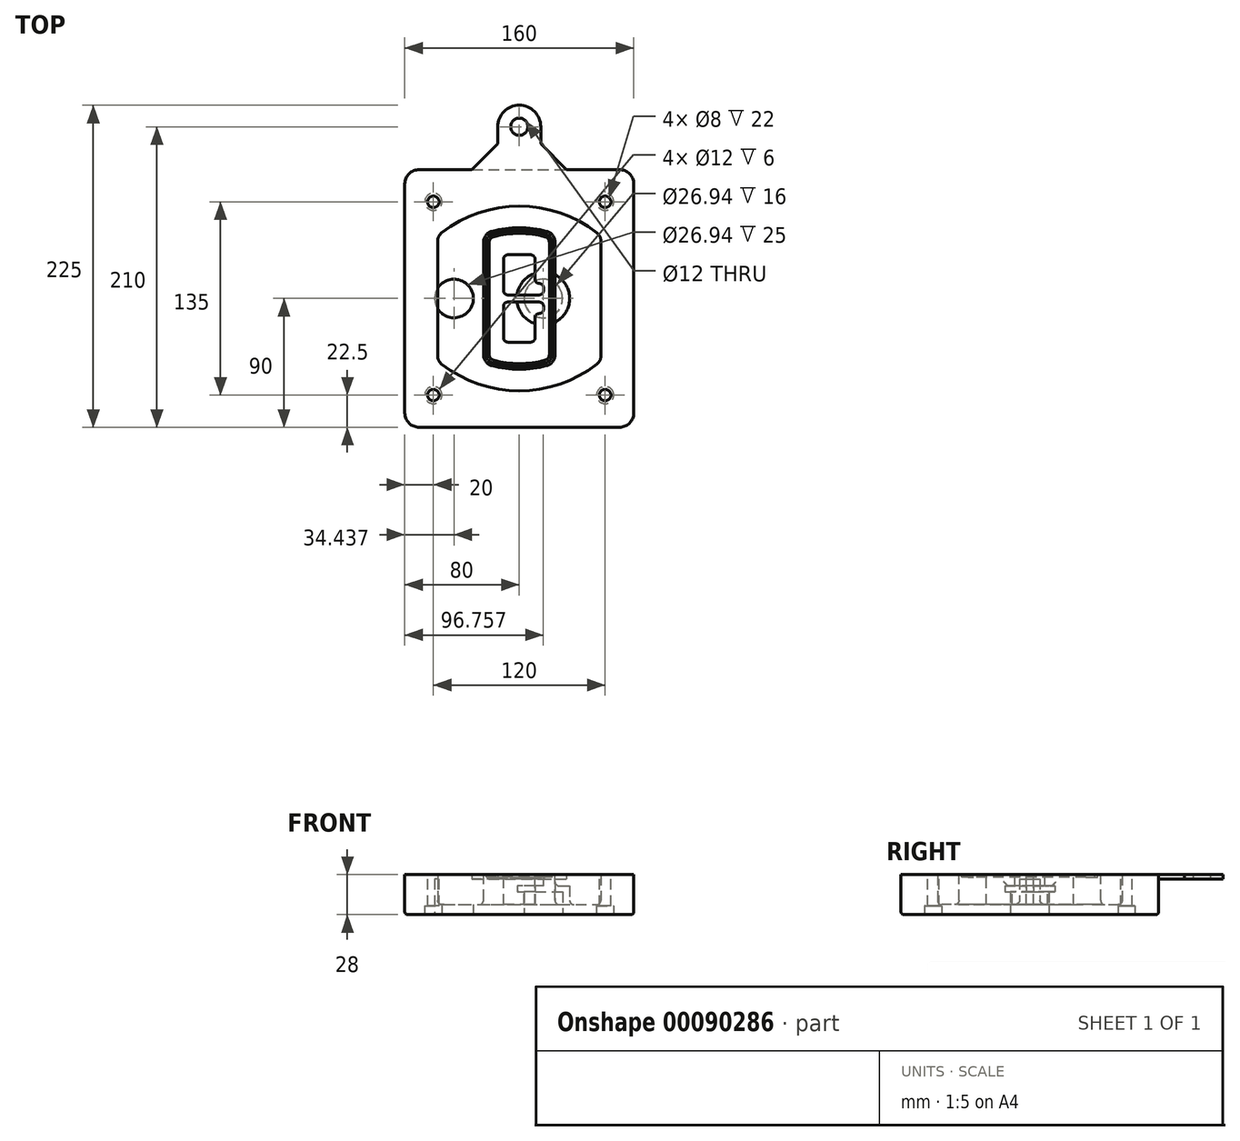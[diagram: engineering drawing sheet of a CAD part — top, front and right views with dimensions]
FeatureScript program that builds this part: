
annotation { "Feature Type Name" : "Feature", "Feature Type Description" : "" }
export const myFeature = defineFeature(function(context is Context, id is Id, definition is map)
    precondition{}
    {
        {
            var Q0;
            Q0=qCreatedBy(makeId("Top.planeOp"),FACE);
            var sketch = newSketch(context, id + "F0", { "sketchPlane" : qUnion([Q0])});
            skPoint(sketch, "E0.rect.middle", {"position": v(0, 0) * mm});
            skLineSegment(sketch, "E1.bottom", {"start": v(-70, -90) * mm, "end": v(70, -90) * mm});
            skLineSegment(sketch, "E1.top", {"start": v(-70, 90) * mm, "end": v(70, 90) * mm});
            skLineSegment(sketch, "E1.left", {"start": v(-80, -80) * mm, "end": v(-80, 80) * mm});
            skLineSegment(sketch, "E1.right", {"start": v(80, -80) * mm, "end": v(80, 80) * mm});
            skLineSegment(sketch, "E2", {"start": v(-80, 90) * mm, "end": v(80, -90) * mm, "construction": true});
            skLineSegment(sketch, "E3", {"start": v(80, 90) * mm, "end": v(-80, -90) * mm, "construction": true});
            skCircle(sketch, "E4", {"center": v(-60, 67.5) * mm, "radius": 4 * mm});
            skCircle(sketch, "E5", {"center": v(60, 67.5) * mm, "radius": 4 * mm});
            skCircle(sketch, "E6", {"center": v(60, -67.5) * mm, "radius": 4 * mm});
            skCircle(sketch, "E7", {"center": v(-60, -67.5) * mm, "radius": 4 * mm});
            skLineSegment(sketch, "E8", {"start": v(-60, 67.5) * mm, "end": v(60, 67.5) * mm, "construction": true});
            skLineSegment(sketch, "E9", {"start": v(60, 67.5) * mm, "end": v(60, -67.5) * mm, "construction": true});
            skLineSegment(sketch, "E10", {"start": v(60, -67.5) * mm, "end": v(-60, -67.5) * mm, "construction": true});
            skLineSegment(sketch, "E11", {"start": v(-60, -67.5) * mm, "end": v(-60, 67.5) * mm, "construction": true});
            skLineSegment(sketch, "E12", {"start": v(-60, 40.3) * mm, "end": v(-60, -40.3) * mm});
            skLineSegment(sketch, "E13", {"start": v(60, 40.3) * mm, "end": v(60, -40.3) * mm});
            skArc(sketch, "E14", {"start": v(56.15, 48.18) * mm, "mid": v(0, 67.5) * mm, "end": v(-56.15, 48.18) * mm});
            skArc(sketch, "E15", {"start": v(-56.15, -48.18) * mm, "mid": v(0, -67.5) * mm, "end": v(56.15, -48.18) * mm});
            skLineSegment(sketch, "E16", {"start": v(-60, 0) * mm, "end": v(60, 0) * mm, "construction": true});
            skPoint(sketch, "E17.visualSharp", {"position": v(-60, -45) * mm});
            skArc(sketch, "E17.filletArc", {"start": v(-60, -40.3) * mm, "mid": v(-58.99, -44.68) * mm, "end": v(-56.15, -48.18) * mm});
            skPoint(sketch, "E18.visualSharp", {"position": v(-60, 45) * mm});
            skArc(sketch, "E18.filletArc", {"start": v(-56.15, 48.18) * mm, "mid": v(-58.99, 44.68) * mm, "end": v(-60, 40.3) * mm});
            skPoint(sketch, "E19.visualSharp", {"position": v(60, 45) * mm});
            skArc(sketch, "E19.filletArc", {"start": v(60, 40.3) * mm, "mid": v(58.99, 44.68) * mm, "end": v(56.15, 48.18) * mm});
            skPoint(sketch, "E20.visualSharp", {"position": v(60, -45) * mm});
            skArc(sketch, "E20.filletArc", {"start": v(56.15, -48.18) * mm, "mid": v(58.99, -44.68) * mm, "end": v(60, -40.3) * mm});
            skPoint(sketch, "E21.visualSharp", {"position": v(-80, 90) * mm});
            skArc(sketch, "E21.filletArc", {"start": v(-70, 90) * mm, "mid": v(-77.07, 87.07) * mm, "end": v(-80, 80) * mm});
            skPoint(sketch, "E22.visualSharp", {"position": v(80, 90) * mm});
            skArc(sketch, "E22.filletArc", {"start": v(80, 80) * mm, "mid": v(77.07, 87.07) * mm, "end": v(70, 90) * mm});
            skPoint(sketch, "E23.visualSharp", {"position": v(80, -90) * mm});
            skArc(sketch, "E23.filletArc", {"start": v(70, -90) * mm, "mid": v(77.07, -87.07) * mm, "end": v(80, -80) * mm});
            skPoint(sketch, "E24.visualSharp", {"position": v(-80, -90) * mm});
            skArc(sketch, "E24.filletArc", {"start": v(-80, -80) * mm, "mid": v(-77.07, -87.07) * mm, "end": v(-70, -90) * mm});
            skArc(sketch, "E25.0", {"start": v(57, 40.3) * mm, "mid": v(56.3, 43.36) * mm, "end": v(54.3, 45.81) * mm});
            skLineSegment(sketch, "E25.1", {"start": v(57, 40.3) * mm, "end": v(57, -40.3) * mm});
            skArc(sketch, "E25.2", {"start": v(54.3, -45.81) * mm, "mid": v(56.3, -43.36) * mm, "end": v(57, -40.3) * mm});
            skArc(sketch, "E25.3", {"start": v(-54.3, -45.81) * mm, "mid": v(0, -64.5) * mm, "end": v(54.3, -45.81) * mm});
            skArc(sketch, "E25.4", {"start": v(-57, -40.3) * mm, "mid": v(-56.3, -43.36) * mm, "end": v(-54.3, -45.81) * mm});
            skArc(sketch, "E25.5", {"start": v(54.3, 45.81) * mm, "mid": v(0, 64.5) * mm, "end": v(-54.3, 45.81) * mm});
            skLineSegment(sketch, "E25.6", {"start": v(-57, 40.3) * mm, "end": v(-57, -40.3) * mm});
            skArc(sketch, "E25.7", {"start": v(-54.3, 45.81) * mm, "mid": v(-56.3, 43.36) * mm, "end": v(-57, 40.3) * mm});
            skArc(sketch, "E26.0", {"start": v(-58.62, 51.33) * mm, "mid": v(-62.58, 46.43) * mm, "end": v(-64, 40.3) * mm});
            skArc(sketch, "E26.1", {"start": v(58.62, 51.33) * mm, "mid": v(0, 71.5) * mm, "end": v(-58.62, 51.33) * mm});
            skArc(sketch, "E26.2", {"start": v(64, 40.3) * mm, "mid": v(62.58, 46.43) * mm, "end": v(58.62, 51.33) * mm});
            skLineSegment(sketch, "E26.3", {"start": v(64, 40.3) * mm, "end": v(64, -40.3) * mm});
            skArc(sketch, "E26.4", {"start": v(58.62, -51.33) * mm, "mid": v(62.58, -46.43) * mm, "end": v(64, -40.3) * mm});
            skLineSegment(sketch, "E26.5", {"start": v(-64, 40.3) * mm, "end": v(-64, -40.3) * mm});
            skArc(sketch, "E26.6", {"start": v(-58.62, -51.33) * mm, "mid": v(0, -71.5) * mm, "end": v(58.62, -51.33) * mm});
            skArc(sketch, "E26.7", {"start": v(-64, -40.3) * mm, "mid": v(-62.58, -46.43) * mm, "end": v(-58.62, -51.33) * mm});
            skSolve(sketch);
        }
        {
            var Q0;
            Q0=makeQuery(id+"F0.imprint","IMPRINT",FACE,{"disambiguationData":[TD([[makeQuery(id+"F0.imprint","IMPRINT",EDGE,{"derivedFrom":sQuery(id+"F0.wireOp",EDGE,"E1.bottom")}),1.0]])]});
            var Q1;
            Q1=makeQuery(id+"F0.imprint","IMPRINT",FACE,{"disambiguationData":[TD([[makeQuery(id+"F0.imprint","IMPRINT",EDGE,{"derivedFrom":sQuery(id+"F0.wireOp",EDGE,"E12")}),1.0]])]});
            var Q2;
            Q2=makeQuery(id+"F0.imprint","IMPRINT",FACE,{"disambiguationData":[TD([[makeQuery(id+"F0.imprint","IMPRINT",EDGE,{"derivedFrom":sQuery(id+"F0.wireOp",EDGE,"E25.0")}),1.0]])]});
            var Q3;
            Q3=makeQuery(id+"F0.imprint","IMPRINT",FACE,{"disambiguationData":[TD([[makeQuery(id+"F0.imprint","IMPRINT",EDGE,{"derivedFrom":sQuery(id+"F0.wireOp",EDGE,"E12")}),-1.0]])]});
            extrude(context, id + "F1", {"entities" : qUnion([Q0, Q1, Q2, Q3]), "oppositeDirection" : true, "depth" : 25 * mm});
        }
        {
            var Q0;
            Q0=makeQuery(id+"F0.imprint","IMPRINT",FACE,{"disambiguationData":[TD([[makeQuery(id+"F0.imprint","IMPRINT",EDGE,{"derivedFrom":sQuery(id+"F0.wireOp",EDGE,"E12")}),1.0]])]});
            extrude(context, id + "F2", {"entities" : qUnion([Q0]), "operationType" : NewBodyOperationType.ADD, "depth" : 3 * mm});
        }
        {
            var Q0;
            Q0=makeQuery(id+"F0.imprint","IMPRINT",FACE,{"disambiguationData":[TD([[makeQuery(id+"F0.imprint","IMPRINT",EDGE,{"derivedFrom":sQuery(id+"F0.wireOp",EDGE,"E25.0")}),1.0]])]});
            extrude(context, id + "F3", {"entities" : qUnion([Q0]), "operationType" : NewBodyOperationType.REMOVE, "oppositeDirection" : true, "depth" : 18 * mm});
        }
        {
            var Q0;
            Q0=makeQuery(id+"F2.opExtrude","CAP_FACE",FACE,{"disambiguationData":[OSD([sQuery(id+"F0.wireOp",EDGE,"E12"),sQuery(id+"F0.wireOp",EDGE,"E13"),sQuery(id+"F0.wireOp",EDGE,"E14"),sQuery(id+"F0.wireOp",EDGE,"E15"),sQuery(id+"F0.wireOp",EDGE,"E17.filletArc"),sQuery(id+"F0.wireOp",EDGE,"E18.filletArc"),sQuery(id+"F0.wireOp",EDGE,"E19.filletArc"),sQuery(id+"F0.wireOp",EDGE,"E20.filletArc"),sQuery(id+"F0.wireOp",EDGE,"E25.0"),sQuery(id+"F0.wireOp",EDGE,"E25.1"),sQuery(id+"F0.wireOp",EDGE,"E25.2"),sQuery(id+"F0.wireOp",EDGE,"E25.3"),sQuery(id+"F0.wireOp",EDGE,"E25.4"),sQuery(id+"F0.wireOp",EDGE,"E25.5"),sQuery(id+"F0.wireOp",EDGE,"E25.6"),sQuery(id+"F0.wireOp",EDGE,"E25.7")])],"isStart":false});
            var sketch = newSketch(context, id + "F4", { "sketchPlane" : qUnion([Q0])});
            skArc(sketch, "E27.0", {"start": v(-19.08, -46.97) * mm, "mid": v(0, -49.5) * mm, "end": v(19.08, -46.97) * mm});
            skArc(sketch, "E28.0", {"start": v(19.08, 46.97) * mm, "mid": v(0, 49.5) * mm, "end": v(-19.08, 46.97) * mm});
            skLineSegment(sketch, "E29", {"start": v(-25, 39.25) * mm, "end": v(-25, -39.25) * mm});
            skLineSegment(sketch, "E30", {"start": v(25, 39.25) * mm, "end": v(25, -39.25) * mm});
            skLineSegment(sketch, "E31", {"start": v(-25, 45.1) * mm, "end": v(25, 45.1) * mm, "construction": true});
            skLineSegment(sketch, "E32", {"start": v(-25, -45.1) * mm, "end": v(25, -45.1) * mm, "construction": true});
            skPoint(sketch, "E33.visualSharp", {"position": v(-25, 45.1) * mm});
            skArc(sketch, "E33.filletArc", {"start": v(-19.08, 46.97) * mm, "mid": v(-23.35, 44.11) * mm, "end": v(-25, 39.25) * mm});
            skPoint(sketch, "E34.visualSharp", {"position": v(25, 45.1) * mm});
            skArc(sketch, "E34.filletArc", {"start": v(25, 39.25) * mm, "mid": v(23.35, 44.11) * mm, "end": v(19.08, 46.97) * mm});
            skPoint(sketch, "E35.visualSharp", {"position": v(25, -45.1) * mm});
            skArc(sketch, "E35.filletArc", {"start": v(19.08, -46.97) * mm, "mid": v(23.35, -44.11) * mm, "end": v(25, -39.25) * mm});
            skPoint(sketch, "E36.visualSharp", {"position": v(-25, -45.1) * mm});
            skArc(sketch, "E36.filletArc", {"start": v(-25, -39.25) * mm, "mid": v(-23.35, -44.11) * mm, "end": v(-19.08, -46.97) * mm});
            skArc(sketch, "E37.0", {"start": v(54.3, 45.81) * mm, "mid": v(0, 64.5) * mm, "end": v(-54.3, 45.81) * mm});
            skArc(sketch, "E37.1", {"start": v(-54.3, 45.81) * mm, "mid": v(-56.3, 43.36) * mm, "end": v(-57, 40.3) * mm});
            skLineSegment(sketch, "E37.2", {"start": v(-57, 40.3) * mm, "end": v(-57, -40.3) * mm});
            skArc(sketch, "E37.3", {"start": v(-57, -40.3) * mm, "mid": v(-56.3, -43.36) * mm, "end": v(-54.3, -45.81) * mm});
            skArc(sketch, "E37.4", {"start": v(-54.3, -45.81) * mm, "mid": v(0, -64.5) * mm, "end": v(54.3, -45.81) * mm});
            skArc(sketch, "E37.5", {"start": v(54.3, -45.81) * mm, "mid": v(56.3, -43.36) * mm, "end": v(57, -40.3) * mm});
            skLineSegment(sketch, "E37.6", {"start": v(57, 40.3) * mm, "end": v(57, -40.3) * mm});
            skArc(sketch, "E37.7", {"start": v(57, 40.3) * mm, "mid": v(56.3, 43.36) * mm, "end": v(54.3, 45.81) * mm});
            skLineSegment(sketch, "E38.0", {"start": v(23, 39.25) * mm, "end": v(23, -39.25) * mm});
            skArc(sketch, "E38.1", {"start": v(18.56, -45.04) * mm, "mid": v(21.76, -42.9) * mm, "end": v(23, -39.25) * mm});
            skArc(sketch, "E38.2", {"start": v(-18.56, -45.04) * mm, "mid": v(0, -47.5) * mm, "end": v(18.56, -45.04) * mm});
            skArc(sketch, "E38.3", {"start": v(-23, -39.25) * mm, "mid": v(-21.76, -42.9) * mm, "end": v(-18.56, -45.04) * mm});
            skLineSegment(sketch, "E38.4", {"start": v(-23, 39.25) * mm, "end": v(-23, -39.25) * mm});
            skArc(sketch, "E38.5", {"start": v(23, 39.25) * mm, "mid": v(21.76, 42.9) * mm, "end": v(18.56, 45.04) * mm});
            skArc(sketch, "E38.6", {"start": v(-18.56, 45.04) * mm, "mid": v(-21.76, 42.9) * mm, "end": v(-23, 39.25) * mm});
            skArc(sketch, "E38.7", {"start": v(18.56, 45.04) * mm, "mid": v(0, 47.5) * mm, "end": v(-18.56, 45.04) * mm});
            skArc(sketch, "E39.0", {"start": v(21, 39.25) * mm, "mid": v(20.18, 41.68) * mm, "end": v(18.04, 43.1) * mm});
            skLineSegment(sketch, "E39.1", {"start": v(21, 39.25) * mm, "end": v(21, -39.25) * mm});
            skArc(sketch, "E39.2", {"start": v(18.04, -43.1) * mm, "mid": v(20.18, -41.68) * mm, "end": v(21, -39.25) * mm});
            skArc(sketch, "E39.3", {"start": v(-18.04, -43.1) * mm, "mid": v(0, -45.5) * mm, "end": v(18.04, -43.1) * mm});
            skArc(sketch, "E39.4", {"start": v(-21, -39.25) * mm, "mid": v(-20.18, -41.68) * mm, "end": v(-18.04, -43.1) * mm});
            skArc(sketch, "E39.5", {"start": v(18.04, 43.1) * mm, "mid": v(0, 45.5) * mm, "end": v(-18.04, 43.1) * mm});
            skLineSegment(sketch, "E39.6", {"start": v(-21, 39.25) * mm, "end": v(-21, -39.25) * mm});
            skArc(sketch, "E39.7", {"start": v(-18.04, 43.1) * mm, "mid": v(-20.18, 41.68) * mm, "end": v(-21, 39.25) * mm});
            skLineSegment(sketch, "E40", {"start": v(-25, 0) * mm, "end": v(25, 0) * mm, "construction": true});
            skLineSegment(sketch, "E41", {"start": v(-11, 5.5) * mm, "end": v(-11, 27.5) * mm});
            skLineSegment(sketch, "E42", {"start": v(-8, 30.5) * mm, "end": v(8, 30.5) * mm});
            skLineSegment(sketch, "E43", {"start": v(11, 27.5) * mm, "end": v(11, 13.5) * mm});
            skLineSegment(sketch, "E44", {"start": v(14, 10.5) * mm, "end": v(14, 10.5) * mm});
            skLineSegment(sketch, "E45", {"start": v(17, 7.5) * mm, "end": v(17, 5.5) * mm});
            skLineSegment(sketch, "E46", {"start": v(14, 2.5) * mm, "end": v(-8, 2.5) * mm});
            skPoint(sketch, "E47.visualSharp", {"position": v(-11, 30.5) * mm});
            skArc(sketch, "E47.filletArc", {"start": v(-8, 30.5) * mm, "mid": v(-10.12, 29.62) * mm, "end": v(-11, 27.5) * mm});
            skPoint(sketch, "E48.visualSharp", {"position": v(11, 30.5) * mm});
            skArc(sketch, "E48.filletArc", {"start": v(11, 27.5) * mm, "mid": v(10.12, 29.62) * mm, "end": v(8, 30.5) * mm});
            skPoint(sketch, "E49.visualSharp", {"position": v(11, 10.5) * mm});
            skArc(sketch, "E49.filletArc", {"start": v(11, 13.5) * mm, "mid": v(11.88, 11.38) * mm, "end": v(14, 10.5) * mm});
            skPoint(sketch, "E50.visualSharp", {"position": v(17, 10.5) * mm});
            skArc(sketch, "E50.filletArc", {"start": v(17, 7.5) * mm, "mid": v(16.12, 9.62) * mm, "end": v(14, 10.5) * mm});
            skPoint(sketch, "E51.visualSharp", {"position": v(17, 2.5) * mm});
            skArc(sketch, "E51.filletArc", {"start": v(14, 2.5) * mm, "mid": v(16.12, 3.38) * mm, "end": v(17, 5.5) * mm});
            skPoint(sketch, "E52.visualSharp", {"position": v(-11, 2.5) * mm});
            skArc(sketch, "E52.filletArc", {"start": v(-11, 5.5) * mm, "mid": v(-10.12, 3.38) * mm, "end": v(-8, 2.5) * mm});
            skLineSegment(sketch, "E53.0.MirrorCS", {"start": v(14, -2.5) * mm, "end": v(-8, -2.5) * mm});
            skArc(sketch, "E54.0.MirrorCS", {"start": v(-11, -5.5) * mm, "mid": v(-10.12, -3.38) * mm, "end": v(-8, -2.5) * mm});
            skLineSegment(sketch, "E55.0.MirrorCS", {"start": v(-11, -5.5) * mm, "end": v(-11, -27.5) * mm});
            skArc(sketch, "E56.0.MirrorCS", {"start": v(-8, -30.5) * mm, "mid": v(-10.12, -29.62) * mm, "end": v(-11, -27.5) * mm});
            skLineSegment(sketch, "E57.0.MirrorCS", {"start": v(-8, -30.5) * mm, "end": v(8, -30.5) * mm});
            skArc(sketch, "E58.0.MirrorCS", {"start": v(11, -27.5) * mm, "mid": v(10.12, -29.62) * mm, "end": v(8, -30.5) * mm});
            skLineSegment(sketch, "E59.0.MirrorCS", {"start": v(11, -27.5) * mm, "end": v(11, -13.5) * mm});
            skArc(sketch, "E60.0.MirrorCS", {"start": v(11, -13.5) * mm, "mid": v(11.88, -11.38) * mm, "end": v(14, -10.5) * mm});
            skArc(sketch, "E61.0.MirrorCS", {"start": v(17, -7.5) * mm, "mid": v(16.12, -9.62) * mm, "end": v(14, -10.5) * mm});
            skLineSegment(sketch, "E62.0.MirrorCS", {"start": v(17, -7.5) * mm, "end": v(17, -5.5) * mm});
            skArc(sketch, "E63.0.MirrorCS", {"start": v(14, -2.5) * mm, "mid": v(16.12, -3.38) * mm, "end": v(17, -5.5) * mm});
            skSolve(sketch);
        }
        {
            var Q0;
            Q0=makeQuery(id+"F4.imprint","IMPRINT",FACE,{"disambiguationData":[TD([[makeQuery(id+"F4.imprint","IMPRINT",EDGE,{"derivedFrom":sQuery(id+"F4.wireOp",EDGE,"E27.0")}),1.0]])]});
            var Q1;
            Q1=makeQuery(id+"F4.imprint","IMPRINT",FACE,{"disambiguationData":[TD([[makeQuery(id+"F4.imprint","IMPRINT",EDGE,{"derivedFrom":sQuery(id+"F4.wireOp",EDGE,"E38.0")}),-1.0]])]});
            var Q2;
            Q2=makeQuery(id+"F4.imprint","IMPRINT",FACE,{"disambiguationData":[TD([[makeQuery(id+"F4.imprint","IMPRINT",EDGE,{"derivedFrom":sQuery(id+"F4.wireOp",EDGE,"E39.0")}),1.0]])]});
            extrude(context, id + "F5", {"entities" : qUnion([Q0, Q1, Q2]), "operationType" : NewBodyOperationType.ADD, "endBound" : BoundingType.UP_TO_NEXT, "oppositeDirection" : true, "depth" : 25 * mm});
        }
        {
            var Q0;
            Q0=makeQuery(id+"F4.imprint","IMPRINT",FACE,{"disambiguationData":[TD([[makeQuery(id+"F4.imprint","IMPRINT",EDGE,{"derivedFrom":sQuery(id+"F4.wireOp",EDGE,"E38.0")}),-1.0]])]});
            extrude(context, id + "F6", {"entities" : qUnion([Q0]), "operationType" : NewBodyOperationType.REMOVE, "oppositeDirection" : true, "depth" : 2 * mm});
        }
        {
            var Q0;
            Q0=makeQuery(id+"F1.opExtrude","CAP_FACE",FACE,{"disambiguationData":[OSD([sQuery(id+"F0.wireOp",EDGE,"E1.bottom"),sQuery(id+"F0.wireOp",EDGE,"E1.top"),sQuery(id+"F0.wireOp",EDGE,"E1.left"),sQuery(id+"F0.wireOp",EDGE,"E1.right"),sQuery(id+"F0.wireOp",EDGE,"E4"),sQuery(id+"F0.wireOp",EDGE,"E5"),sQuery(id+"F0.wireOp",EDGE,"E6"),sQuery(id+"F0.wireOp",EDGE,"E7"),sQuery(id+"F0.wireOp",EDGE,"E21.filletArc"),sQuery(id+"F0.wireOp",EDGE,"E22.filletArc"),sQuery(id+"F0.wireOp",EDGE,"E23.filletArc"),sQuery(id+"F0.wireOp",EDGE,"E24.filletArc")])],"isStart":false});
            var sketch = newSketch(context, id + "F7", { "sketchPlane" : qUnion([Q0])});
            skCircle(sketch, "E64", {"center": v(16.76, 0) * mm, "radius": 13.47 * mm});
            skCircle(sketch, "E65", {"center": v(-45.56, 0) * mm, "radius": 13.47 * mm});
            skLineSegment(sketch, "E66", {"start": v(80, 0) * mm, "end": v(-80, 0) * mm});
            skCircle(sketch, "E67", {"center": v(16.76, 0) * mm, "radius": 18.47 * mm});
            skCircle(sketch, "E68", {"center": v(60, -67.5) * mm, "radius": 6 * mm});
            skCircle(sketch, "E69", {"center": v(-60, -67.5) * mm, "radius": 6 * mm});
            skCircle(sketch, "E70", {"center": v(-60, 67.5) * mm, "radius": 6 * mm});
            skCircle(sketch, "E71", {"center": v(60, 67.5) * mm, "radius": 6 * mm});
            skSolve(sketch);
        }
        {
            var Q0;
            {var subQ1=sQuery(id+"F7.wireOp",EDGE,"E66");var subQ4=sQuery(id+"F7.wireOp",EDGE,"E64");var subQ6=makeQuery(id+"F7.imprint","INTERSECT",VERTEX,{"disambiguationData":[OD(0.0)],"derivedFrom":[subQ4,subQ1]});Q0=makeQuery(id+"F7.imprint","IMPRINT",FACE,{"disambiguationData":[TD([[makeQuery(id+"F7.imprint","IMPRINT",EDGE,{"disambiguationData":[TD([[subQ6,-1.0]])],"derivedFrom":subQ4}),-1.0]])]});}
            var Q1;
            {var subQ0=sQuery(id+"F7.wireOp",EDGE,"E66");var subQ1=sQuery(id+"F7.wireOp",EDGE,"E64");var subQ3=makeQuery(id+"F7.imprint","INTERSECT",VERTEX,{"disambiguationData":[OD(0.0)],"derivedFrom":[subQ1,subQ0]});Q1=makeQuery(id+"F7.imprint","IMPRINT",FACE,{"disambiguationData":[TD([[makeQuery(id+"F7.imprint","IMPRINT",EDGE,{"disambiguationData":[TD([[subQ3,-1.0]])],"derivedFrom":subQ1}),1.0]])]});}
            var Q2;
            {var subQ0=sQuery(id+"F7.wireOp",EDGE,"E66");var subQ1=sQuery(id+"F7.wireOp",EDGE,"E64");var subQ3=makeQuery(id+"F7.imprint","INTERSECT",VERTEX,{"disambiguationData":[OD(0.0)],"derivedFrom":[subQ1,subQ0]});Q2=makeQuery(id+"F7.imprint","IMPRINT",FACE,{"disambiguationData":[TD([[makeQuery(id+"F7.imprint","IMPRINT",EDGE,{"disambiguationData":[TD([[subQ3,1.0]])],"derivedFrom":subQ1}),1.0]])]});}
            var Q3;
            {var subQ1=sQuery(id+"F7.wireOp",EDGE,"E66");var subQ4=sQuery(id+"F7.wireOp",EDGE,"E64");var subQ6=makeQuery(id+"F7.imprint","INTERSECT",VERTEX,{"disambiguationData":[OD(0.0)],"derivedFrom":[subQ4,subQ1]});Q3=makeQuery(id+"F7.imprint","IMPRINT",FACE,{"disambiguationData":[TD([[makeQuery(id+"F7.imprint","IMPRINT",EDGE,{"disambiguationData":[TD([[subQ6,1.0]])],"derivedFrom":subQ4}),-1.0]])]});}
            extrude(context, id + "F8", {"entities" : qUnion([Q0, Q1, Q2, Q3]), "operationType" : NewBodyOperationType.ADD, "oppositeDirection" : true, "depth" : 20 * mm});
        }
        {
            var Q0;
            {var subQ0=sQuery(id+"F7.wireOp",EDGE,"E66");var subQ1=sQuery(id+"F7.wireOp",EDGE,"E64");var subQ3=makeQuery(id+"F7.imprint","INTERSECT",VERTEX,{"disambiguationData":[OD(0.0)],"derivedFrom":[subQ1,subQ0]});Q0=makeQuery(id+"F7.imprint","IMPRINT",FACE,{"disambiguationData":[TD([[makeQuery(id+"F7.imprint","IMPRINT",EDGE,{"disambiguationData":[TD([[subQ3,-1.0]])],"derivedFrom":subQ1}),1.0]])]});}
            var Q1;
            {var subQ0=sQuery(id+"F7.wireOp",EDGE,"E66");var subQ1=sQuery(id+"F7.wireOp",EDGE,"E64");var subQ3=makeQuery(id+"F7.imprint","INTERSECT",VERTEX,{"disambiguationData":[OD(0.0)],"derivedFrom":[subQ1,subQ0]});Q1=makeQuery(id+"F7.imprint","IMPRINT",FACE,{"disambiguationData":[TD([[makeQuery(id+"F7.imprint","IMPRINT",EDGE,{"disambiguationData":[TD([[subQ3,1.0]])],"derivedFrom":subQ1}),1.0]])]});}
            extrude(context, id + "F9", {"entities" : qUnion([Q0, Q1]), "operationType" : NewBodyOperationType.REMOVE, "oppositeDirection" : true, "depth" : 16 * mm});
        }
        {
            var Q0;
            {var subQ0=sQuery(id+"F7.wireOp",EDGE,"E66");var subQ1=sQuery(id+"F7.wireOp",EDGE,"E65");var subQ3=makeQuery(id+"F7.imprint","INTERSECT",VERTEX,{"disambiguationData":[OD(0.0)],"derivedFrom":[subQ1,subQ0]});Q0=makeQuery(id+"F7.imprint","IMPRINT",FACE,{"disambiguationData":[TD([[makeQuery(id+"F7.imprint","IMPRINT",EDGE,{"disambiguationData":[TD([[subQ3,-1.0]])],"derivedFrom":subQ1}),1.0]])]});}
            var Q1;
            {var subQ0=sQuery(id+"F7.wireOp",EDGE,"E66");var subQ1=sQuery(id+"F7.wireOp",EDGE,"E65");var subQ3=makeQuery(id+"F7.imprint","INTERSECT",VERTEX,{"disambiguationData":[OD(0.0)],"derivedFrom":[subQ1,subQ0]});Q1=makeQuery(id+"F7.imprint","IMPRINT",FACE,{"disambiguationData":[TD([[makeQuery(id+"F7.imprint","IMPRINT",EDGE,{"disambiguationData":[TD([[subQ3,1.0]])],"derivedFrom":subQ1}),1.0]])]});}
            extrude(context, id + "F10", {"entities" : qUnion([Q0, Q1]), "operationType" : NewBodyOperationType.REMOVE, "oppositeDirection" : true, "depth" : 25 * mm});
        }
        {
            var Q0;
            Q0=makeQuery(id+"F7.imprint","IMPRINT",FACE,{"disambiguationData":[TD([[makeQuery(id+"F7.imprint","IMPRINT",EDGE,{"derivedFrom":sQuery(id+"F7.wireOp",EDGE,"E68")}),1.0]])]});
            var Q1;
            Q1=makeQuery(id+"F7.imprint","IMPRINT",FACE,{"disambiguationData":[TD([[makeQuery(id+"F7.imprint","IMPRINT",EDGE,{"derivedFrom":makeQuery(id+"F1.opExtrude","CAP_EDGE",EDGE,{"disambiguationData":[OSD([sQuery(id+"F0.wireOp",EDGE,"E5")])],"isStart":false})}),-1.0]])]});
            var Q2;
            Q2=makeQuery(id+"F7.imprint","IMPRINT",FACE,{"disambiguationData":[TD([[makeQuery(id+"F7.imprint","IMPRINT",EDGE,{"derivedFrom":sQuery(id+"F7.wireOp",EDGE,"E69")}),1.0]])]});
            var Q3;
            Q3=makeQuery(id+"F7.imprint","IMPRINT",FACE,{"disambiguationData":[TD([[makeQuery(id+"F7.imprint","IMPRINT",EDGE,{"derivedFrom":makeQuery(id+"F1.opExtrude","CAP_EDGE",EDGE,{"disambiguationData":[OSD([sQuery(id+"F0.wireOp",EDGE,"E4")])],"isStart":false})}),-1.0]])]});
            var Q4;
            Q4=makeQuery(id+"F7.imprint","IMPRINT",FACE,{"disambiguationData":[TD([[makeQuery(id+"F7.imprint","IMPRINT",EDGE,{"derivedFrom":sQuery(id+"F7.wireOp",EDGE,"E70")}),1.0]])]});
            var Q5;
            Q5=makeQuery(id+"F7.imprint","IMPRINT",FACE,{"disambiguationData":[TD([[makeQuery(id+"F7.imprint","IMPRINT",EDGE,{"derivedFrom":makeQuery(id+"F1.opExtrude","CAP_EDGE",EDGE,{"disambiguationData":[OSD([sQuery(id+"F0.wireOp",EDGE,"E7")])],"isStart":false})}),-1.0]])]});
            var Q6;
            Q6=makeQuery(id+"F7.imprint","IMPRINT",FACE,{"disambiguationData":[TD([[makeQuery(id+"F7.imprint","IMPRINT",EDGE,{"derivedFrom":sQuery(id+"F7.wireOp",EDGE,"E71")}),1.0]])]});
            var Q7;
            Q7=makeQuery(id+"F7.imprint","IMPRINT",FACE,{"disambiguationData":[TD([[makeQuery(id+"F7.imprint","IMPRINT",EDGE,{"derivedFrom":makeQuery(id+"F1.opExtrude","CAP_EDGE",EDGE,{"disambiguationData":[OSD([sQuery(id+"F0.wireOp",EDGE,"E6")])],"isStart":false})}),-1.0]])]});
            extrude(context, id + "F11", {"entities" : qUnion([Q0, Q1, Q2, Q3, Q4, Q5, Q6, Q7]), "operationType" : NewBodyOperationType.REMOVE, "oppositeDirection" : true, "depth" : 6 * mm});
        }
        {
            var Q0;
            Q0=makeQuery(id+"F9.boolean.opBoolean","COPY",FACE,{"derivedFrom":makeQuery(id+"F9.opExtrude","CAP_FACE",FACE,{"disambiguationData":[OSD([sQuery(id+"F7.wireOp",EDGE,"E64")])],"isStart":false})});
            var sketch = newSketch(context, id + "F12", { "sketchPlane" : qUnion([Q0])});
            skArc(sketch, "E72.0", {"start": v(11, 17.55) * mm, "mid": v(2.57, 11.82) * mm, "end": v(-1.54, 2.5) * mm});
            skArc(sketch, "E72.1", {"start": v(-1.54, -2.5) * mm, "mid": v(2.57, -11.82) * mm, "end": v(11, -17.55) * mm});
            skLineSegment(sketch, "E73", {"start": v(-1.54, -2.5) * mm, "end": v(14, -2.5) * mm});
            skLineSegment(sketch, "E74.0", {"start": v(14, 2.5) * mm, "end": v(-1.54, 2.5) * mm});
            skArc(sketch, "E74.1", {"start": v(14, 2.5) * mm, "mid": v(16.12, 3.38) * mm, "end": v(17, 5.5) * mm});
            skLineSegment(sketch, "E74.2", {"start": v(17, 7.5) * mm, "end": v(17, 5.5) * mm});
            skArc(sketch, "E74.3", {"start": v(17, 7.5) * mm, "mid": v(16.12, 9.62) * mm, "end": v(14, 10.5) * mm});
            skArc(sketch, "E74.4", {"start": v(11, 13.5) * mm, "mid": v(11.88, 11.38) * mm, "end": v(14, 10.5) * mm});
            skLineSegment(sketch, "E74.5", {"start": v(11, 17.55) * mm, "end": v(11, 13.5) * mm});
            skLineSegment(sketch, "E74.7", {"start": v(14, -2.5) * mm, "end": v(-1.54, -2.5) * mm});
            skArc(sketch, "E74.8", {"start": v(14, -2.5) * mm, "mid": v(16.12, -3.38) * mm, "end": v(17, -5.5) * mm});
            skLineSegment(sketch, "E74.9", {"start": v(17, -7.5) * mm, "end": v(17, -5.5) * mm});
            skArc(sketch, "E74.10", {"start": v(17, -7.5) * mm, "mid": v(16.12, -9.62) * mm, "end": v(14, -10.5) * mm});
            skArc(sketch, "E74.11", {"start": v(11, -13.5) * mm, "mid": v(11.88, -11.38) * mm, "end": v(14, -10.5) * mm});
            skLineSegment(sketch, "E74.12", {"start": v(11, -17.55) * mm, "end": v(11, -13.5) * mm});
            skPoint(sketch, "E75.orphan", {"position": v(11, -27.5) * mm});
            skPoint(sketch, "E76.orphan", {"position": v(-8, -2.5) * mm});
            skPoint(sketch, "E77.orphan", {"position": v(-8, 2.5) * mm});
            skPoint(sketch, "E78.orphan", {"position": v(11, 27.5) * mm});
            skSolve(sketch);
        }
        {
            var Q0;
            {var subQ7=sQuery(id+"F12.wireOp",EDGE,"E72.0");var subQ14=sQuery(id+"F12.wireOp",EDGE,"E72.1");var subQ16=sQuery(id+"F12.wireOp",EDGE,"E74.1");var subQ18=sQuery(id+"F12.wireOp",EDGE,"E74.8");Q0=qUnion([makeQuery(id+"F12.imprint","IMPRINT",FACE,{"disambiguationData":[TD([[makeQuery(id+"F12.imprint","IMPRINT",EDGE,{"derivedFrom":subQ7}),1.0]])]}),makeQuery(id+"F12.imprint","IMPRINT",FACE,{"disambiguationData":[TD([[makeQuery(id+"F12.imprint","IMPRINT",EDGE,{"derivedFrom":subQ14}),1.0]])]}),makeQuery(id+"F12.imprint","IMPRINT",FACE,{"disambiguationData":[TD([[makeQuery(id+"F12.imprint","IMPRINT",EDGE,{"derivedFrom":subQ16}),1.0]])]}),makeQuery(id+"F12.imprint","IMPRINT",FACE,{"disambiguationData":[TD([[makeQuery(id+"F12.imprint","IMPRINT",EDGE,{"derivedFrom":subQ18}),-1.0]])]})]);}
            var Q1;
            Q1=makeQuery(id+"F5.boolean.opBoolean","SPLIT",FACE,{"disambiguationData":[TD([makeQuery(id+"F5.opExtrude","SWEPT_FACE",FACE,{"disambiguationData":[OSD([sQuery(id+"F4.wireOp",EDGE,"E41")])]})])],"derivedFrom":makeQuery(id+"F3.boolean.opBoolean","COPY",FACE,{"derivedFrom":makeQuery(id+"F3.opExtrude","CAP_FACE",FACE,{"disambiguationData":[OSD([sQuery(id+"F0.wireOp",EDGE,"E25.0"),sQuery(id+"F0.wireOp",EDGE,"E25.1"),sQuery(id+"F0.wireOp",EDGE,"E25.2"),sQuery(id+"F0.wireOp",EDGE,"E25.3"),sQuery(id+"F0.wireOp",EDGE,"E25.4"),sQuery(id+"F0.wireOp",EDGE,"E25.5"),sQuery(id+"F0.wireOp",EDGE,"E25.6"),sQuery(id+"F0.wireOp",EDGE,"E25.7")])],"isStart":false})})});
            extrude(context, id + "F13", {"entities" : qUnion([Q0]), "operationType" : NewBodyOperationType.REMOVE, "endBound" : BoundingType.UP_TO_SURFACE, "endBoundEntityFace" : qUnion([Q1]), "depth" : 25 * mm});
        }
        {
            var Q0;
            Q0=makeQuery(id+"F3.boolean.opBoolean","COPY",EDGE,{"derivedFrom":makeQuery(id+"F3.opExtrude","CAP_EDGE",EDGE,{"disambiguationData":[OSD([sQuery(id+"F0.wireOp",EDGE,"E25.6")])],"isStart":false})});
            var Q1;
            Q1=makeQuery(id+"F8.boolean.opBoolean","INTERSECT",EDGE,{"derivedFrom":[makeQuery(id+"F5.opExtrude","SWEPT_FACE",FACE,{"disambiguationData":[OSD([sQuery(id+"F4.wireOp",EDGE,"E30")])]}),makeQuery(id+"F8.opExtrude","CAP_FACE",FACE,{"disambiguationData":[OSD([sQuery(id+"F7.wireOp",EDGE,"E67")])],"isStart":false})]});
            var Q2;
            Q2=makeQuery(id+"F8.boolean.opBoolean","INTERSECT",EDGE,{"disambiguationData":[OD(1.0)],"derivedFrom":[makeQuery(id+"F5.opExtrude","SWEPT_FACE",FACE,{"disambiguationData":[OSD([sQuery(id+"F4.wireOp",EDGE,"E30")])]}),makeQuery(id+"F8.opExtrude","SWEPT_FACE",FACE,{"disambiguationData":[OSD([sQuery(id+"F7.wireOp",EDGE,"E67")])]})]});
            var Q3;
            {var subQ0=sQuery(id+"F4.wireOp",EDGE,"E30");Q3=makeQuery(id+"F8.boolean.opBoolean","SPLIT",EDGE,{"disambiguationData":[TD([makeQuery(id+"F5.opExtrude","SWEPT_FACE",FACE,{"disambiguationData":[OSD([sQuery(id+"F4.wireOp",EDGE,"E35.filletArc")])]})])],"derivedFrom":makeQuery(id+"F5.opExtrude","CAP_EDGE",EDGE,{"disambiguationData":[OSD([subQ0])],"isStart":false})});}
            var Q4;
            {var subQ0=sQuery(id+"F0.wireOp",EDGE,"E25.7");var subQ1=sQuery(id+"F0.wireOp",EDGE,"E25.1");var subQ2=sQuery(id+"F0.wireOp",EDGE,"E25.6");var subQ3=sQuery(id+"F0.wireOp",EDGE,"E25.5");var subQ4=sQuery(id+"F0.wireOp",EDGE,"E25.4");var subQ5=sQuery(id+"F0.wireOp",EDGE,"E25.0");var subQ6=sQuery(id+"F0.wireOp",EDGE,"E25.2");var subQ7=sQuery(id+"F0.wireOp",EDGE,"E25.3");Q4=makeQuery(id+"F8.boolean.opBoolean","INTERSECT",EDGE,{"derivedFrom":[makeQuery(id+"F5.boolean.opBoolean","SPLIT",FACE,{"disambiguationData":[TD([makeQuery(id+"F2.opExtrude","SWEPT_FACE",FACE,{"disambiguationData":[OSD([subQ5])]})])],"derivedFrom":makeQuery(id+"F3.boolean.opBoolean","COPY",FACE,{"derivedFrom":makeQuery(id+"F3.opExtrude","CAP_FACE",FACE,{"disambiguationData":[OSD([subQ5,subQ1,subQ6,subQ7,subQ4,subQ3,subQ2,subQ0])],"isStart":false})})}),makeQuery(id+"F8.opExtrude","SWEPT_FACE",FACE,{"disambiguationData":[OSD([sQuery(id+"F7.wireOp",EDGE,"E67")])]})]});}
            var Q5;
            Q5=makeQuery(id+"F8.boolean.opBoolean","INTERSECT",EDGE,{"disambiguationData":[OD(0.0)],"derivedFrom":[makeQuery(id+"F5.opExtrude","SWEPT_FACE",FACE,{"disambiguationData":[OSD([sQuery(id+"F4.wireOp",EDGE,"E30")])]}),makeQuery(id+"F8.opExtrude","SWEPT_FACE",FACE,{"disambiguationData":[OSD([sQuery(id+"F7.wireOp",EDGE,"E67")])]})]});
            fillet(context, id + "F14", {"entities" : qUnion([Q0, Q1, Q2, Q3, Q4, Q5]), "radius" : 3 * mm, "tangentPropagation" : true, "allowEdgeOverflow" : false});
        }
        {
            var Q0;
            Q0=makeQuery(id+"F1.opExtrude","CAP_EDGE",EDGE,{"disambiguationData":[OSD([sQuery(id+"F0.wireOp",EDGE,"E1.bottom")])],"isStart":false});
            fillet(context, id + "F15", {"entities" : qUnion([Q0]), "radius" : 2 * mm, "tangentPropagation" : true, "allowEdgeOverflow" : false});
        }
        {
            var Q0;
            {var subQ0=sQuery(id+"F0.wireOp",EDGE,"E22.filletArc");var subQ1=sQuery(id+"F0.wireOp",EDGE,"E7");var subQ2=sQuery(id+"F0.wireOp",EDGE,"E6");var subQ3=sQuery(id+"F0.wireOp",EDGE,"E5");var subQ4=sQuery(id+"F0.wireOp",EDGE,"E4");var subQ5=sQuery(id+"F0.wireOp",EDGE,"E1.bottom");var subQ6=sQuery(id+"F0.wireOp",EDGE,"E21.filletArc");var subQ7=sQuery(id+"F0.wireOp",EDGE,"E1.top");var subQ8=sQuery(id+"F0.wireOp",EDGE,"E1.left");var subQ9=sQuery(id+"F0.wireOp",EDGE,"E1.right");var subQ10=sQuery(id+"F0.wireOp",EDGE,"E23.filletArc");var subQ11=sQuery(id+"F0.wireOp",EDGE,"E24.filletArc");Q0=makeQuery(id+"F2.boolean.opBoolean","SPLIT",FACE,{"disambiguationData":[TD([makeQuery(id+"F1.opExtrude","SWEPT_FACE",FACE,{"disambiguationData":[OSD([subQ5])]})])],"derivedFrom":makeQuery(id+"F1.opExtrude","CAP_FACE",FACE,{"disambiguationData":[OSD([subQ5,subQ7,subQ8,subQ9,subQ4,subQ3,subQ2,subQ1,subQ6,subQ0,subQ10,subQ11])],"isStart":true})});}
            var sketch = newSketch(context, id + "F16", { "sketchPlane" : qUnion([Q0])});
            skLineSegment(sketch, "E79", {"start": v(0, 90) * mm, "end": v(0, 120) * mm, "construction": true});
            skCircle(sketch, "E80", {"center": v(0, 120) * mm, "radius": 6 * mm});
            skArc(sketch, "E81", {"start": v(15, 120) * mm, "mid": v(0, 135) * mm, "end": v(-15, 120) * mm});
            skLineSegment(sketch, "E82", {"start": v(-15, 120) * mm, "end": v(-15, 108) * mm});
            skLineSegment(sketch, "E83", {"start": v(-15, 108) * mm, "end": v(-33, 90) * mm});
            skLineSegment(sketch, "E84", {"start": v(15, 120) * mm, "end": v(15, 108) * mm});
            skLineSegment(sketch, "E85", {"start": v(15, 108) * mm, "end": v(33, 90) * mm});
            skLineSegment(sketch, "E86", {"start": v(0, 120) * mm, "end": v(0, 0) * mm, "construction": true});
            skArc(sketch, "E87.MirrorCS", {"start": v(15, -120) * mm, "mid": v(0, -135) * mm, "end": v(-15, -120) * mm});
            skLineSegment(sketch, "E88.MirrorCS", {"start": v(0, -120) * mm, "end": v(0, 0) * mm, "construction": true});
            skLineSegment(sketch, "E89.MirrorCS", {"start": v(0, -90) * mm, "end": v(0, -120) * mm, "construction": true});
            skLineSegment(sketch, "E90.MirrorCS", {"start": v(-15, -120) * mm, "end": v(-15, -108) * mm});
            skLineSegment(sketch, "E91.MirrorCS", {"start": v(-15, -108) * mm, "end": v(-33, -90) * mm});
            skLineSegment(sketch, "E92.MirrorCS", {"start": v(15, -108) * mm, "end": v(33, -90) * mm});
            skLineSegment(sketch, "E93.MirrorCS", {"start": v(15, -120) * mm, "end": v(15, -108) * mm});
            skCircle(sketch, "E94.MirrorC", {"center": v(0, -120) * mm, "radius": 6 * mm});
            skSolve(sketch);
        }
        {
            var Q0;
            Q0=makeQuery(id+"F16.imprint","IMPRINT",FACE,{"disambiguationData":[TD([[makeQuery(id+"F16.imprint","IMPRINT",EDGE,{"derivedFrom":sQuery(id+"F16.wireOp",EDGE,"E80")}),-1.0]])]});
            var Q1;
            Q1=makeQuery(id+"F16.imprint","IMPRINT",FACE,{"disambiguationData":[TD([[makeQuery(id+"F16.imprint","IMPRINT",EDGE,{"derivedFrom":makeQuery(id+"F1.opExtrude","CAP_EDGE",EDGE,{"disambiguationData":[OSD([sQuery(id+"F0.wireOp",EDGE,"E1.left")])],"isStart":true})}),-1.0]])]});
            var Q2;
            Q2=makeQuery(id+"F16.imprint","IMPRINT",FACE,{"disambiguationData":[TD([[makeQuery(id+"F16.imprint","IMPRINT",EDGE,{"derivedFrom":sQuery(id+"F16.wireOp",EDGE,"E87.MirrorCS")}),-1.0]])]});
            var Q3;
            Q3=makeQuery(id+"F2.opExtrude","CAP_FACE",FACE,{"disambiguationData":[OSD([sQuery(id+"F0.wireOp",EDGE,"E12"),sQuery(id+"F0.wireOp",EDGE,"E13"),sQuery(id+"F0.wireOp",EDGE,"E14"),sQuery(id+"F0.wireOp",EDGE,"E15"),sQuery(id+"F0.wireOp",EDGE,"E17.filletArc"),sQuery(id+"F0.wireOp",EDGE,"E18.filletArc"),sQuery(id+"F0.wireOp",EDGE,"E19.filletArc"),sQuery(id+"F0.wireOp",EDGE,"E20.filletArc"),sQuery(id+"F0.wireOp",EDGE,"E25.0"),sQuery(id+"F0.wireOp",EDGE,"E25.1"),sQuery(id+"F0.wireOp",EDGE,"E25.2"),sQuery(id+"F0.wireOp",EDGE,"E25.3"),sQuery(id+"F0.wireOp",EDGE,"E25.4"),sQuery(id+"F0.wireOp",EDGE,"E25.5"),sQuery(id+"F0.wireOp",EDGE,"E25.6"),sQuery(id+"F0.wireOp",EDGE,"E25.7")])],"isStart":false});
            extrude(context, id + "F17", {"entities" : qUnion([Q0, Q1, Q2]), "operationType" : NewBodyOperationType.ADD, "endBound" : BoundingType.UP_TO_SURFACE, "endBoundEntityFace" : qUnion([Q3]), "depth" : 25 * mm});
        }
    });
